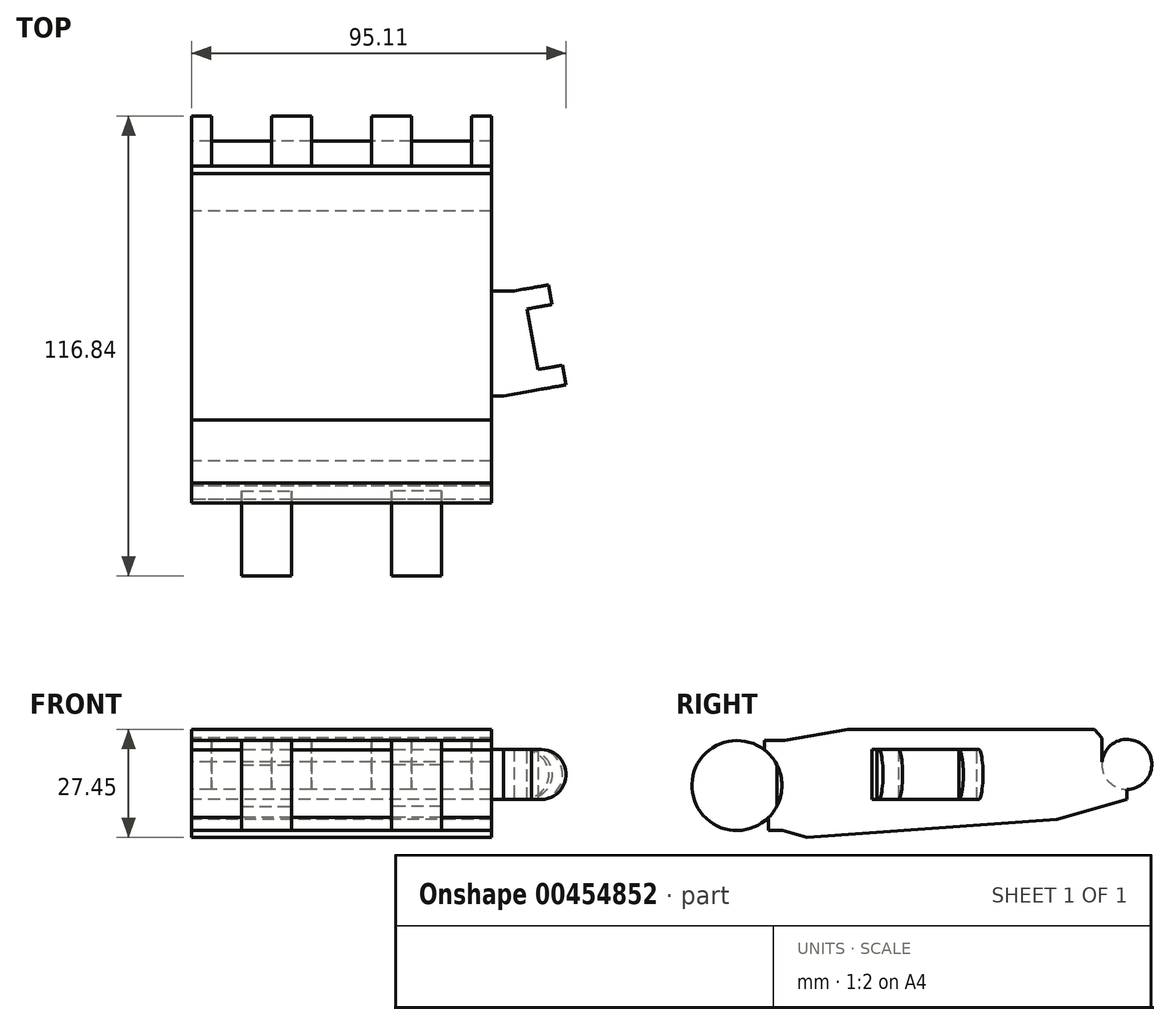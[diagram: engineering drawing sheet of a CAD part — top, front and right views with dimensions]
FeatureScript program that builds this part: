
annotation { "Feature Type Name" : "Feature", "Feature Type Description" : "" }
export const myFeature = defineFeature(function(context is Context, id is Id, definition is map)
    precondition{}
    {
        {
            var Q0;
            Q0=qCreatedBy(makeId("Right.planeOp"),FACE);
            var sketch = newSketch(context, id + "F0", { "sketchPlane" : qUnion([Q0])});
            skLineSegment(sketch, "E0.bottom", {"start": v(36.15, 14) * mm, "end": v(-44.45, 14) * mm});
            skLineSegment(sketch, "E0.left", {"start": v(44.45, 11.46) * mm, "end": v(44.45, -3.78) * mm});
            skLineSegment(sketch, "E0.right", {"start": v(-44.45, 14) * mm, "end": v(-44.45, -14) * mm});
            skPoint(sketch, "E0.middle", {"position": v(0, 0) * mm});
            skLineSegment(sketch, "E1.bottom", {"start": v(-44.45, 11.17) * mm, "end": v(-47.56, 11.17) * mm});
            skLineSegment(sketch, "E1.top", {"start": v(-44.45, -11.7) * mm, "end": v(-46.56, -11.7) * mm});
            skLineSegment(sketch, "E1.left", {"start": v(-44.45, 11.17) * mm, "end": v(-44.45, -11.7) * mm});
            skLineSegment(sketch, "E1.right", {"start": v(-54.61, 11.17) * mm, "end": v(-54.6, -11.7) * mm});
            skCircle(sketch, "E2", {"center": v(-54.61, -0.26) * mm, "radius": 11.43 * mm});
            skLineSegment(sketch, "E3", {"start": v(44.45, -3.78) * mm, "end": v(26.67, -8.9) * mm});
            skPoint(sketch, "E3.endSnap0", {"position": v(0, -8.9) * mm});
            skLineSegment(sketch, "E4", {"start": v(26.67, -8.9) * mm, "end": v(-44.45, -14) * mm});
            skPoint(sketch, "E0.top.start.orphan", {"position": v(44.45, -14) * mm});
            skLineSegment(sketch, "E5", {"start": v(-46.56, -8.38) * mm, "end": v(-46.56, -11.7) * mm});
            skLineSegment(sketch, "E6", {"start": v(-47.56, 11.17) * mm, "end": v(-47.56, 8.74) * mm});
            skCircle(sketch, "E7", {"center": v(44.45, 5.1) * mm, "radius": 6.35 * mm});
            skLineSegment(sketch, "E8", {"start": v(38.13, 11.87) * mm, "end": v(36.15, 14) * mm});
            skPoint(sketch, "E9.orphan", {"position": v(44.45, 14) * mm});
            skLineSegment(sketch, "E10", {"start": v(38.13, 11.87) * mm, "end": v(38.13, 5.7) * mm});
            skPoint(sketch, "E11.orphan", {"position": v(40.1, 9.74) * mm});
            skSolve(sketch);
        }
        {
            var Q0;
            {var subQ0=sQuery(id+"F0.wireOp",EDGE,"E1.bottom");Q0=makeQuery(id+"F0.imprint","IMPRINT",FACE,{"disambiguationData":[TD([[makeQuery(id+"F0.imprint","IMPRINT",EDGE,{"derivedFrom":subQ0}),1.0]])]});}
            var Q1;
            {var subQ0=sQuery(id+"F0.wireOp",EDGE,"E1.top");Q1=makeQuery(id+"F0.imprint","IMPRINT",FACE,{"disambiguationData":[TD([[makeQuery(id+"F0.imprint","IMPRINT",EDGE,{"derivedFrom":subQ0}),-1.0]])]});}
            var Q2;
            {var subQ4=sQuery(id+"F0.wireOp",EDGE,"E0.bottom");Q2=makeQuery(id+"F0.imprint","IMPRINT",FACE,{"disambiguationData":[TD([[makeQuery(id+"F0.imprint","IMPRINT",EDGE,{"derivedFrom":subQ4}),1.0]])]});}
            extrude(context, id + "F1", {"entities" : qUnion([Q0, Q1, Q2]), "endBound" : BoundingType.SYMMETRIC, "depth" : 76.2 * mm, "offsetDistance" : 25.4 * mm});
        }
        {
            var Q0;
            Q0=makeQuery(id+"F1.opExtrude","SWEPT_EDGE",EDGE,{"disambiguationData":[OSD([sQuery(id+"F0.wireOp",EDGE,"E0.bottom"),sQuery(id+"F0.wireOp",EDGE,"E0.right")])]});
            chamfer(context, id + "F2", {"entities" : qUnion([Q0]), "chamferType" : ChamferType.OFFSET_ANGLE, "width" : 3.17 * mm, "oppositeDirection" : false, "angle" : 80 * degree, "tangentPropagation" : true});
        }
        {
            var Q0;
            Q0=makeQuery(id+"F1.opExtrude","SWEPT_EDGE",EDGE,{"disambiguationData":[OSD([sQuery(id+"F0.wireOp",EDGE,"E0.right"),sQuery(id+"F0.wireOp",EDGE,"E4")])]});
            chamfer(context, id + "F3", {"entities" : qUnion([Q0]), "chamferType" : ChamferType.OFFSET_ANGLE, "width" : 7.62 * mm, "oppositeDirection" : false, "angle" : 20 * degree, "tangentPropagation" : true});
        }
        {
            var Q0;
            {var subQ0=sQuery(id+"F0.wireOp",EDGE,"E2");var subQ1=sQuery(id+"F0.wireOp",EDGE,"E1.left");var subQ2=makeQuery(id+"F0.imprint","INTERSECT",VERTEX,{"disambiguationData":[OD(0.0)],"derivedFrom":[subQ1,subQ0]});Q0=makeQuery(id+"F0.imprint","IMPRINT",FACE,{"disambiguationData":[TD([[makeQuery(id+"F0.imprint","IMPRINT",EDGE,{"disambiguationData":[TD([[subQ2,-1.0]])],"derivedFrom":subQ1}),1.0]])]});}
            var Q1;
            {var subQ1=sQuery(id+"F0.wireOp",EDGE,"E1.right");Q1=makeQuery(id+"F0.imprint","IMPRINT",FACE,{"disambiguationData":[TD([[makeQuery(id+"F0.imprint","IMPRINT",EDGE,{"derivedFrom":subQ1}),1.0]])]});}
            var Q2;
            {var subQ0=sQuery(id+"F0.wireOp",EDGE,"E1.right");Q2=makeQuery(id+"F0.imprint","IMPRINT",FACE,{"disambiguationData":[TD([[makeQuery(id+"F0.imprint","IMPRINT",EDGE,{"derivedFrom":subQ0}),-1.0]])]});}
            extrude(context, id + "F4", {"entities" : qUnion([Q0, Q1, Q2]), "operationType" : NewBodyOperationType.ADD, "depth" : 25.4 * mm, "offsetDistance" : 25.4 * mm, "hasSecondDirection" : true, "secondDirectionOppositeDirection" : false, "secondDirectionDepth" : 12.7 * mm});
        }
        {
            var Q0;
            {var subQ0=sQuery(id+"F0.wireOp",EDGE,"E2");var subQ1=sQuery(id+"F0.wireOp",EDGE,"E1.left");var subQ2=makeQuery(id+"F0.imprint","INTERSECT",VERTEX,{"disambiguationData":[OD(0.0)],"derivedFrom":[subQ1,subQ0]});Q0=makeQuery(id+"F0.imprint","IMPRINT",FACE,{"disambiguationData":[TD([[makeQuery(id+"F0.imprint","IMPRINT",EDGE,{"disambiguationData":[TD([[subQ2,-1.0]])],"derivedFrom":subQ1}),1.0]])]});}
            var Q1;
            {var subQ1=sQuery(id+"F0.wireOp",EDGE,"E1.right");Q1=makeQuery(id+"F0.imprint","IMPRINT",FACE,{"disambiguationData":[TD([[makeQuery(id+"F0.imprint","IMPRINT",EDGE,{"derivedFrom":subQ1}),1.0]])]});}
            var Q2;
            {var subQ0=sQuery(id+"F0.wireOp",EDGE,"E1.right");Q2=makeQuery(id+"F0.imprint","IMPRINT",FACE,{"disambiguationData":[TD([[makeQuery(id+"F0.imprint","IMPRINT",EDGE,{"derivedFrom":subQ0}),-1.0]])]});}
            extrude(context, id + "F5", {"entities" : qUnion([Q0, Q1, Q2]), "operationType" : NewBodyOperationType.ADD, "oppositeDirection" : true, "depth" : 25.4 * mm, "offsetDistance" : 25.4 * mm, "hasSecondDirection" : true, "secondDirectionOppositeDirection" : true, "secondDirectionDepth" : 12.7 * mm});
        }
        {
            var Q0;
            {var subQ0=sQuery(id+"F0.wireOp",EDGE,"E7");var subQ1=sQuery(id+"F0.wireOp",EDGE,"E0.left");var subQ2=makeQuery(id+"F0.imprint","INTERSECT",VERTEX,{"disambiguationData":[OD(0.0)],"derivedFrom":[subQ1,subQ0]});Q0=makeQuery(id+"F0.imprint","IMPRINT",FACE,{"disambiguationData":[TD([[makeQuery(id+"F0.imprint","IMPRINT",EDGE,{"disambiguationData":[TD([[subQ2,-1.0]])],"derivedFrom":subQ1}),1.0]])]});}
            var Q1;
            {var subQ0=sQuery(id+"F0.wireOp",EDGE,"E7");var subQ1=sQuery(id+"F0.wireOp",EDGE,"E0.left");var subQ2=makeQuery(id+"F0.imprint","INTERSECT",VERTEX,{"disambiguationData":[OD(0.0)],"derivedFrom":[subQ1,subQ0]});Q1=makeQuery(id+"F0.imprint","IMPRINT",FACE,{"disambiguationData":[TD([[makeQuery(id+"F0.imprint","IMPRINT",EDGE,{"disambiguationData":[TD([[subQ2,-1.0]])],"derivedFrom":subQ1}),-1.0]])]});}
            extrude(context, id + "F6", {"entities" : qUnion([Q0, Q1]), "operationType" : NewBodyOperationType.ADD, "depth" : 38.1 * mm, "offsetDistance" : 25.4 * mm, "hasSecondDirection" : true, "secondDirectionOppositeDirection" : false, "secondDirectionDepth" : 33.02 * mm});
        }
        {
            var Q0;
            {var subQ0=sQuery(id+"F0.wireOp",EDGE,"E7");var subQ1=sQuery(id+"F0.wireOp",EDGE,"E0.left");var subQ2=makeQuery(id+"F0.imprint","INTERSECT",VERTEX,{"disambiguationData":[OD(0.0)],"derivedFrom":[subQ1,subQ0]});Q0=makeQuery(id+"F0.imprint","IMPRINT",FACE,{"disambiguationData":[TD([[makeQuery(id+"F0.imprint","IMPRINT",EDGE,{"disambiguationData":[TD([[subQ2,-1.0]])],"derivedFrom":subQ1}),1.0]])]});}
            var Q1;
            {var subQ0=sQuery(id+"F0.wireOp",EDGE,"E7");var subQ1=sQuery(id+"F0.wireOp",EDGE,"E0.left");var subQ2=makeQuery(id+"F0.imprint","INTERSECT",VERTEX,{"disambiguationData":[OD(0.0)],"derivedFrom":[subQ1,subQ0]});Q1=makeQuery(id+"F0.imprint","IMPRINT",FACE,{"disambiguationData":[TD([[makeQuery(id+"F0.imprint","IMPRINT",EDGE,{"disambiguationData":[TD([[subQ2,-1.0]])],"derivedFrom":subQ1}),-1.0]])]});}
            extrude(context, id + "F7", {"entities" : qUnion([Q0, Q1]), "operationType" : NewBodyOperationType.ADD, "depth" : 17.78 * mm, "offsetDistance" : 25.4 * mm, "hasSecondDirection" : true, "secondDirectionOppositeDirection" : false, "secondDirectionDepth" : 12.7 * mm});
        }
        {
            var Q0;
            {var subQ0=sQuery(id+"F0.wireOp",EDGE,"E7");var subQ1=sQuery(id+"F0.wireOp",EDGE,"E0.left");var subQ2=makeQuery(id+"F0.imprint","INTERSECT",VERTEX,{"disambiguationData":[OD(0.0)],"derivedFrom":[subQ1,subQ0]});Q0=makeQuery(id+"F0.imprint","IMPRINT",FACE,{"disambiguationData":[TD([[makeQuery(id+"F0.imprint","IMPRINT",EDGE,{"disambiguationData":[TD([[subQ2,-1.0]])],"derivedFrom":subQ1}),1.0]])]});}
            var Q1;
            {var subQ0=sQuery(id+"F0.wireOp",EDGE,"E7");var subQ1=sQuery(id+"F0.wireOp",EDGE,"E0.left");var subQ2=makeQuery(id+"F0.imprint","INTERSECT",VERTEX,{"disambiguationData":[OD(0.0)],"derivedFrom":[subQ1,subQ0]});Q1=makeQuery(id+"F0.imprint","IMPRINT",FACE,{"disambiguationData":[TD([[makeQuery(id+"F0.imprint","IMPRINT",EDGE,{"disambiguationData":[TD([[subQ2,-1.0]])],"derivedFrom":subQ1}),-1.0]])]});}
            extrude(context, id + "F8", {"entities" : qUnion([Q0, Q1]), "operationType" : NewBodyOperationType.ADD, "depth" : 12.7 * mm, "offsetDistance" : 25.4 * mm, "hasSecondDirection" : true, "secondDirectionOppositeDirection" : false, "secondDirectionDepth" : 7.62 * mm});
        }
        {
            var Q0;
            {var subQ0=sQuery(id+"F0.wireOp",EDGE,"E7");var subQ1=sQuery(id+"F0.wireOp",EDGE,"E0.left");var subQ2=makeQuery(id+"F0.imprint","INTERSECT",VERTEX,{"disambiguationData":[OD(0.0)],"derivedFrom":[subQ1,subQ0]});Q0=makeQuery(id+"F0.imprint","IMPRINT",FACE,{"disambiguationData":[TD([[makeQuery(id+"F0.imprint","IMPRINT",EDGE,{"disambiguationData":[TD([[subQ2,-1.0]])],"derivedFrom":subQ1}),1.0]])]});}
            var Q1;
            {var subQ0=sQuery(id+"F0.wireOp",EDGE,"E7");var subQ1=sQuery(id+"F0.wireOp",EDGE,"E0.left");var subQ2=makeQuery(id+"F0.imprint","INTERSECT",VERTEX,{"disambiguationData":[OD(0.0)],"derivedFrom":[subQ1,subQ0]});Q1=makeQuery(id+"F0.imprint","IMPRINT",FACE,{"disambiguationData":[TD([[makeQuery(id+"F0.imprint","IMPRINT",EDGE,{"disambiguationData":[TD([[subQ2,-1.0]])],"derivedFrom":subQ1}),-1.0]])]});}
            extrude(context, id + "F9", {"entities" : qUnion([Q0, Q1]), "operationType" : NewBodyOperationType.ADD, "oppositeDirection" : true, "depth" : 12.7 * mm, "offsetDistance" : 25.4 * mm, "hasSecondDirection" : true, "secondDirectionOppositeDirection" : true, "secondDirectionDepth" : 7.62 * mm});
        }
        {
            var Q0;
            {var subQ0=sQuery(id+"F0.wireOp",EDGE,"E7");var subQ1=sQuery(id+"F0.wireOp",EDGE,"E0.left");var subQ2=makeQuery(id+"F0.imprint","INTERSECT",VERTEX,{"disambiguationData":[OD(0.0)],"derivedFrom":[subQ1,subQ0]});Q0=makeQuery(id+"F0.imprint","IMPRINT",FACE,{"disambiguationData":[TD([[makeQuery(id+"F0.imprint","IMPRINT",EDGE,{"disambiguationData":[TD([[subQ2,-1.0]])],"derivedFrom":subQ1}),1.0]])]});}
            var Q1;
            {var subQ0=sQuery(id+"F0.wireOp",EDGE,"E7");var subQ1=sQuery(id+"F0.wireOp",EDGE,"E0.left");var subQ2=makeQuery(id+"F0.imprint","INTERSECT",VERTEX,{"disambiguationData":[OD(0.0)],"derivedFrom":[subQ1,subQ0]});Q1=makeQuery(id+"F0.imprint","IMPRINT",FACE,{"disambiguationData":[TD([[makeQuery(id+"F0.imprint","IMPRINT",EDGE,{"disambiguationData":[TD([[subQ2,-1.0]])],"derivedFrom":subQ1}),-1.0]])]});}
            extrude(context, id + "F10", {"entities" : qUnion([Q0, Q1]), "operationType" : NewBodyOperationType.ADD, "oppositeDirection" : true, "depth" : 17.78 * mm, "offsetDistance" : 25.4 * mm, "hasSecondDirection" : true, "secondDirectionOppositeDirection" : true, "secondDirectionDepth" : 12.7 * mm});
        }
        {
            var Q0;
            {var subQ0=sQuery(id+"F0.wireOp",EDGE,"E7");var subQ1=sQuery(id+"F0.wireOp",EDGE,"E0.left");var subQ2=makeQuery(id+"F0.imprint","INTERSECT",VERTEX,{"disambiguationData":[OD(0.0)],"derivedFrom":[subQ1,subQ0]});Q0=makeQuery(id+"F0.imprint","IMPRINT",FACE,{"disambiguationData":[TD([[makeQuery(id+"F0.imprint","IMPRINT",EDGE,{"disambiguationData":[TD([[subQ2,-1.0]])],"derivedFrom":subQ1}),-1.0]])]});}
            var Q1;
            {var subQ0=sQuery(id+"F0.wireOp",EDGE,"E7");var subQ1=sQuery(id+"F0.wireOp",EDGE,"E0.left");var subQ2=makeQuery(id+"F0.imprint","INTERSECT",VERTEX,{"disambiguationData":[OD(0.0)],"derivedFrom":[subQ1,subQ0]});Q1=makeQuery(id+"F0.imprint","IMPRINT",FACE,{"disambiguationData":[TD([[makeQuery(id+"F0.imprint","IMPRINT",EDGE,{"disambiguationData":[TD([[subQ2,-1.0]])],"derivedFrom":subQ1}),1.0]])]});}
            extrude(context, id + "F11", {"entities" : qUnion([Q0, Q1]), "operationType" : NewBodyOperationType.ADD, "oppositeDirection" : true, "depth" : 38.1 * mm, "offsetDistance" : 25.4 * mm, "hasSecondDirection" : true, "secondDirectionOppositeDirection" : true, "secondDirectionDepth" : 33.02 * mm});
        }
        {
            var Q0;
            {var subQ0=sQuery(id+"F0.wireOp",EDGE,"E7");Q0=makeQuery(id+"F6.boolean.opBoolean","MERGE",FACE,{"derivedFrom":[makeQuery(id+"F1.opExtrude","CAP_FACE",FACE,{"disambiguationData":[OSD([sQuery(id+"F0.wireOp",EDGE,"E0.bottom"),sQuery(id+"F0.wireOp",EDGE,"E0.left"),sQuery(id+"F0.wireOp",EDGE,"E0.right"),sQuery(id+"F0.wireOp",EDGE,"E1.bottom"),sQuery(id+"F0.wireOp",EDGE,"E1.top"),sQuery(id+"F0.wireOp",EDGE,"E2"),sQuery(id+"F0.wireOp",EDGE,"E3"),sQuery(id+"F0.wireOp",EDGE,"E4"),sQuery(id+"F0.wireOp",EDGE,"E5"),sQuery(id+"F0.wireOp",EDGE,"E6"),subQ0])],"isStart":false}),makeQuery(id+"F6.opExtrude","CAP_FACE",FACE,{"disambiguationData":[OSD([subQ0])],"isStart":false})]});}
            var sketch = newSketch(context, id + "F12", { "sketchPlane" : qUnion([Q0])});
            skLineSegment(sketch, "E12.bottom", {"start": v(6.35, -3.78) * mm, "end": v(-19.05, -3.78) * mm});
            skLineSegment(sketch, "E12.top", {"start": v(6.35, 8.92) * mm, "end": v(-19.05, 8.92) * mm});
            skLineSegment(sketch, "E12.left", {"start": v(6.35, -3.78) * mm, "end": v(6.35, 8.92) * mm});
            skLineSegment(sketch, "E12.right", {"start": v(-19.05, -3.78) * mm, "end": v(-19.05, 8.92) * mm});
            skSolve(sketch);
        }
        {
            var Q0;
            Q0=qSketchRegion(id+"F12",true);
            extrude(context, id + "F13", {"entities" : qUnion([Q0]), "operationType" : NewBodyOperationType.ADD, "depth" : 10.16 * mm, "offsetDistance" : 25.4 * mm});
        }
        {
            var Q0;
            Q0=makeQuery(id+"F13.opExtrude","CAP_EDGE",EDGE,{"disambiguationData":[OSD([sQuery(id+"F12.wireOp",EDGE,"E12.left")])],"isStart":false});
            chamfer(context, id + "F14", {"entities" : qUnion([Q0]), "chamferType" : ChamferType.OFFSET_ANGLE, "width" : 25.4 * mm, "oppositeDirection" : false, "angle" : 10 * degree, "tangentPropagation" : true});
        }
        {
            var Q0;
            Q0=makeQuery(id+"F14.opChamfer","BLEND_FACE",FACE,{"disambiguationData":[OSD([sQuery(id+"F12.wireOp",EDGE,"E12.left")])]});
            var sketch = newSketch(context, id + "F15", { "sketchPlane" : qUnion([Q0])});
            skLineSegment(sketch, "E13.bottom", {"start": v(-27.14, 8.92) * mm, "end": v(-1.35, 8.92) * mm});
            skLineSegment(sketch, "E13.top", {"start": v(-27.14, -3.78) * mm, "end": v(-1.35, -3.78) * mm});
            skLineSegment(sketch, "E13.left", {"start": v(-27.14, 8.92) * mm, "end": v(-27.14, -3.78) * mm});
            skLineSegment(sketch, "E13.right", {"start": v(-1.35, 8.92) * mm, "end": v(-1.35, -3.78) * mm});
            skSolve(sketch);
        }
        {
            var Q0;
            Q0 = qSketchRegion(id + "F15", true);
            extrude(context, id + "F16", {"entities" : qUnion([Q0]), "operationType" : NewBodyOperationType.ADD, "depth" : 2.54 * mm, "offsetDistance" : 25.4 * mm});
        }
        {
            var Q0;
            Q0=makeQuery(id+"F16.opExtrude","SWEPT_FACE",FACE,{"disambiguationData":[OSD([sQuery(id+"F15.wireOp",EDGE,"E13.left")])]});
            var sketch = newSketch(context, id + "F17", { "sketchPlane" : qUnion([Q0])});
            skCircle(sketch, "E14", {"center": v(46.76, 2.57) * mm, "radius": 6.35 * mm});
            skSolve(sketch);
        }
        {
            var Q0;
            Q0 = qSketchRegion(id + "F17", true);
            extrude(context, id + "F18", {"entities" : qUnion([Q0]), "operationType" : NewBodyOperationType.ADD, "oppositeDirection" : true, "depth" : 5.08 * mm, "offsetDistance" : 25.4 * mm});
        }
        {
            var Q0;
            Q0=makeQuery(id+"F13.opExtrude","SWEPT_FACE",FACE,{"disambiguationData":[OSD([sQuery(id+"F12.wireOp",EDGE,"E12.right")])]});
            var sketch = newSketch(context, id + "F19", { "sketchPlane" : qUnion([Q0])});
            skLineSegment(sketch, "E15.bottom", {"start": v(38.1, -3.78) * mm, "end": v(48.26, -3.78) * mm});
            skLineSegment(sketch, "E15.top", {"start": v(38.1, 8.92) * mm, "end": v(48.26, 8.92) * mm});
            skLineSegment(sketch, "E15.left", {"start": v(38.1, -3.78) * mm, "end": v(38.1, 8.92) * mm});
            skLineSegment(sketch, "E15.right", {"start": v(48.26, -3.78) * mm, "end": v(48.26, 8.92) * mm});
            skSolve(sketch);
        }
        {
            var Q0;
            Q0 = qSketchRegion(id + "F19", true);
            extrude(context, id + "F20", {"entities" : qUnion([Q0]), "operationType" : NewBodyOperationType.ADD, "depth" : 1.27 * mm, "offsetDistance" : 25.4 * mm});
        }
        {
            var Q0;
            Q0=makeQuery(id+"F20.opExtrude","CAP_EDGE",EDGE,{"disambiguationData":[OSD([sQuery(id+"F19.wireOp",EDGE,"E15.right")])],"isStart":false});
            chamfer(context, id + "F21", {"entities" : qUnion([Q0]), "chamferType" : ChamferType.OFFSET_ANGLE, "width" : 7.11 * mm, "oppositeDirection" : false, "angle" : 10 * degree, "tangentPropagation" : true});
        }
        {
            var Q0;
            Q0=makeQuery(id+"F16.opExtrude","SWEPT_FACE",FACE,{"disambiguationData":[OSD([sQuery(id+"F15.wireOp",EDGE,"E13.right")])]});
            var sketch = newSketch(context, id + "F22", { "sketchPlane" : qUnion([Q0])});
            skCircle(sketch, "E16", {"center": v(-46.76, 2.57) * mm, "radius": 6.35 * mm});
            skSolve(sketch);
        }
        {
            var Q0;
            Q0 = qSketchRegion(id + "F22", true);
            extrude(context, id + "F23", {"entities" : qUnion([Q0]), "operationType" : NewBodyOperationType.ADD, "oppositeDirection" : true, "depth" : 5.08 * mm, "offsetDistance" : 25.4 * mm});
        }
    });
